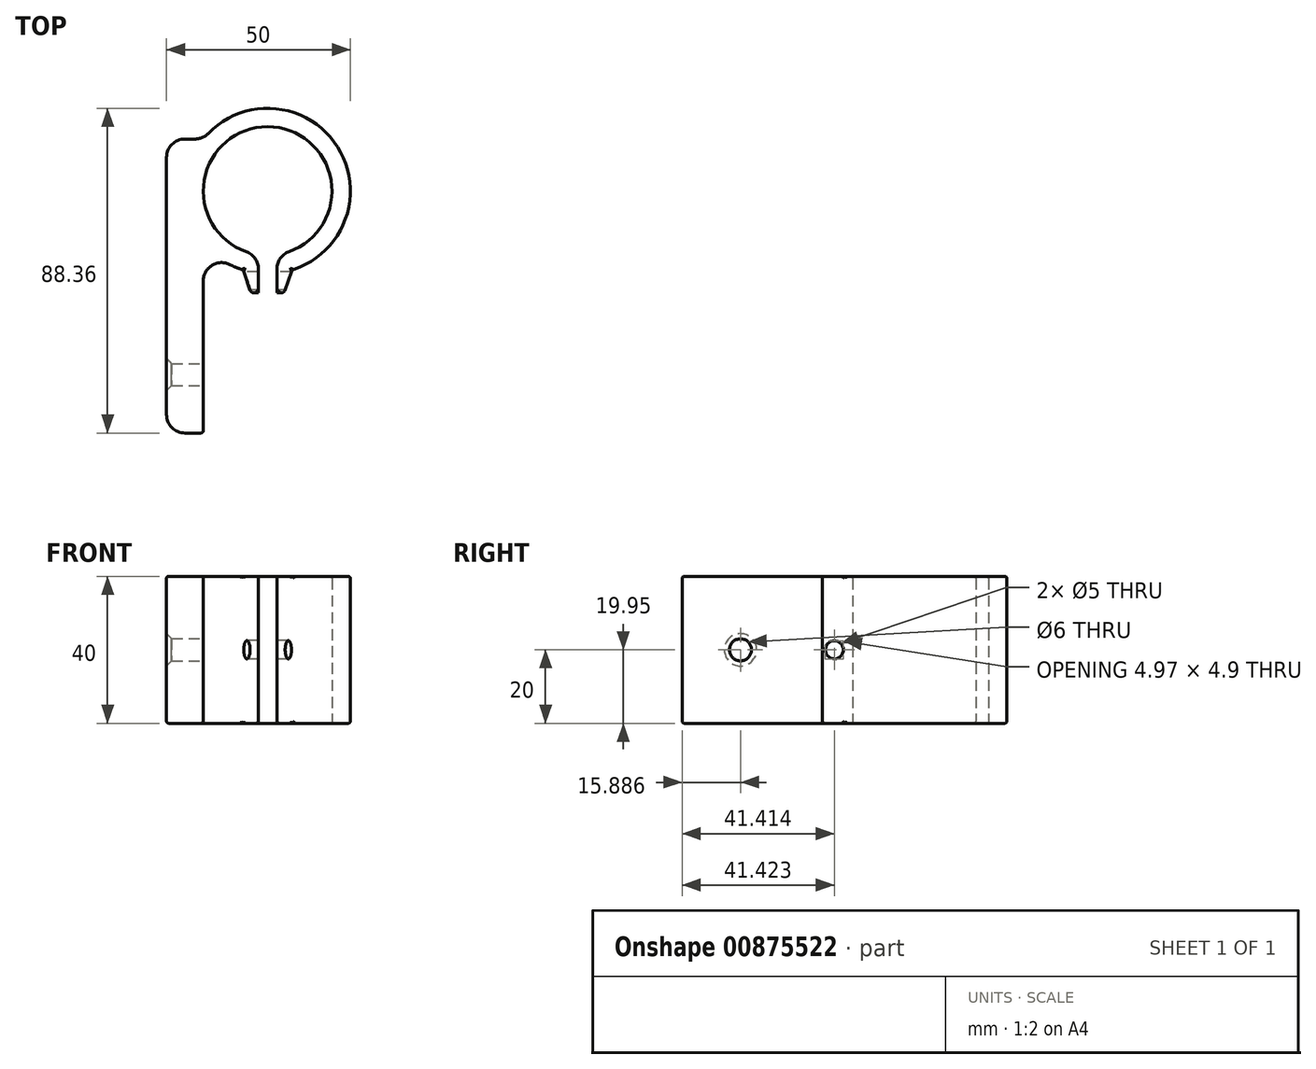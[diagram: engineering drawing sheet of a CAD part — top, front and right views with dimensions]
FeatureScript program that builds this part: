
annotation { "Feature Type Name" : "Feature", "Feature Type Description" : "" }
export const myFeature = defineFeature(function(context is Context, id is Id, definition is map)
    precondition{}
    {
        {
            var Q0;
            Q0=qCreatedBy(makeId("Top.planeOp"),FACE);
            var sketch = newSketch(context, id + "F0", { "sketchPlane" : qUnion([Q0])});
            skLineSegment(sketch, "E0.left", {"start": v(-72.65, -0.58) * mm, "end": v(-72.65, -1.73) * mm});
            skLineSegment(sketch, "E0.right", {"start": v(-77.68, -0.58) * mm, "end": v(-77.68, -7.05) * mm});
            skArc(sketch, "E1", {"start": v(-69.32, 4.13) * mm, "mid": v(-75.17, 38.13) * mm, "end": v(-81.01, 4.13) * mm});
            skLineSegment(sketch, "E2", {"start": v(-72.65, -1.73) * mm, "end": v(-72.65, -7.05) * mm});
            skArc(sketch, "E3", {"start": v(-72.65, -1.73) * mm, "mid": v(-54.97, 30.55) * mm, "end": v(-91.32, 36.29) * mm});
            skLineSegment(sketch, "E4", {"start": v(-72.65, -7.05) * mm, "end": v(-70.65, -7.05) * mm});
            skLineSegment(sketch, "E5", {"start": v(-77.68, -7.05) * mm, "end": v(-79.68, -7.05) * mm});
            skLineSegment(sketch, "E6", {"start": v(-79.68, -7.05) * mm, "end": v(-81.8, -0.87) * mm});
            skLineSegment(sketch, "E7", {"start": v(-70.65, -7.05) * mm, "end": v(-68.52, -0.87) * mm});
            skArc(sketch, "E8", {"start": v(-85.4, 0.59) * mm, "mid": v(-81.64, -0.92) * mm, "end": v(-77.68, -1.73) * mm});
            skLineSegment(sketch, "E9", {"start": v(-95.7, 11.42) * mm, "end": v(-95.7, 29.83) * mm});
            skLineSegment(sketch, "E10", {"start": v(-92.67, 20.63) * mm, "end": v(-92.67, 34.77) * mm});
            skPoint(sketch, "E10.startSnap0", {"position": v(-95.7, 20.63) * mm});
            skLineSegment(sketch, "E11", {"start": v(-92.67, 20.63) * mm, "end": v(-92.67, 6.49) * mm});
            skLineSegment(sketch, "E12.bottom", {"start": v(-94.91, 34.77) * mm, "end": v(-97.67, 34.77) * mm});
            skLineSegment(sketch, "E12.top", {"start": v(-92.67, -45.23) * mm, "end": v(-97.67, -45.23) * mm});
            skLineSegment(sketch, "E12.left", {"start": v(-92.67, -3.87) * mm, "end": v(-92.67, -45.23) * mm});
            skLineSegment(sketch, "E12.right", {"start": v(-102.67, 29.77) * mm, "end": v(-102.67, -40.23) * mm});
            skPoint(sketch, "E13.visualSharp", {"position": v(-102.67, 34.77) * mm});
            skArc(sketch, "E13.filletArc", {"start": v(-97.67, 34.77) * mm, "mid": v(-101.2, 33.3) * mm, "end": v(-102.67, 29.77) * mm});
            skArc(sketch, "E14.filletArc", {"start": v(-94.91, 34.77) * mm, "mid": v(-92.96, 35.17) * mm, "end": v(-91.32, 36.29) * mm});
            skArc(sketch, "E15.filletArc", {"start": v(-85.4, 0.59) * mm, "mid": v(-90.28, 0.4) * mm, "end": v(-92.67, -3.87) * mm});
            skPoint(sketch, "E16.visualSharp", {"position": v(-72.65, 3.31) * mm});
            skArc(sketch, "E16.filletArc", {"start": v(-69.32, 4.13) * mm, "mid": v(-71.73, 2.3) * mm, "end": v(-72.65, -0.58) * mm});
            skPoint(sketch, "E17.visualSharp", {"position": v(-77.68, 3.31) * mm});
            skArc(sketch, "E17.filletArc", {"start": v(-77.68, -0.58) * mm, "mid": v(-78.6, 2.3) * mm, "end": v(-81.01, 4.13) * mm});
            skPoint(sketch, "E18.visualSharp", {"position": v(-102.67, -45.23) * mm});
            skArc(sketch, "E18.filletArc", {"start": v(-102.67, -40.23) * mm, "mid": v(-101.2, -43.77) * mm, "end": v(-97.67, -45.23) * mm});
            skLineSegment(sketch, "E19.left", {"start": v(-92.67, -45.23) * mm, "end": v(-92.67, -41.23) * mm});
            skLineSegment(sketch, "E20.left", {"start": v(-92.67, -41.23) * mm, "end": v(-92.67, -16.23) * mm});
            skLineSegment(sketch, "E21.left", {"start": v(-92.67, -16.23) * mm, "end": v(-92.67, -12.23) * mm});
            skLineSegment(sketch, "E22.left", {"start": v(-92.67, -16.23) * mm, "end": v(-92.67, -41.23) * mm});
            skSolve(sketch);
        }
        {
            var Q0;
            {var subQ0=sQuery(id+"F0.wireOp",EDGE,"E5");Q0=makeQuery(id+"F0.imprint","IMPRINT",FACE,{"disambiguationData":[TD([[makeQuery(id+"F0.imprint","IMPRINT",EDGE,{"derivedFrom":subQ0}),-1.0]])]});}
            var Q1;
            {var subQ0=sQuery(id+"F0.wireOp",EDGE,"E2");Q1=makeQuery(id+"F0.imprint","IMPRINT",FACE,{"disambiguationData":[TD([[makeQuery(id+"F0.imprint","IMPRINT",EDGE,{"derivedFrom":subQ0}),1.0]])]});}
            var Q2;
            {var subQ6=sQuery(id+"F0.wireOp",EDGE,"E0.left");Q2=makeQuery(id+"F0.imprint","IMPRINT",FACE,{"disambiguationData":[TD([[makeQuery(id+"F0.imprint","IMPRINT",EDGE,{"derivedFrom":subQ6}),1.0]])]});}
            extrude(context, id + "F1", {"entities" : qUnion([Q0, Q1, Q2]), "depth" : 40 * mm, "offsetDistance" : 25 * mm});
        }
        {
            var Q0;
            Q0=makeQuery(id+"F1.opExtrude","CAP_FACE",FACE,{"disambiguationData":[OSD([sQuery(id+"F0.wireOp",EDGE,"E0.left"),sQuery(id+"F0.wireOp",EDGE,"E0.right"),sQuery(id+"F0.wireOp",EDGE,"E1"),sQuery(id+"F0.wireOp",EDGE,"E2"),sQuery(id+"F0.wireOp",EDGE,"E3"),sQuery(id+"F0.wireOp",EDGE,"E4"),sQuery(id+"F0.wireOp",EDGE,"E5"),sQuery(id+"F0.wireOp",EDGE,"E6"),sQuery(id+"F0.wireOp",EDGE,"E7"),sQuery(id+"F0.wireOp",EDGE,"E8"),sQuery(id+"F0.wireOp",EDGE,"E12.bottom"),sQuery(id+"F0.wireOp",EDGE,"E12.top"),sQuery(id+"F0.wireOp",EDGE,"E12.left"),sQuery(id+"F0.wireOp",EDGE,"E12.right"),sQuery(id+"F0.wireOp",EDGE,"E13.filletArc"),sQuery(id+"F0.wireOp",EDGE,"E14.filletArc"),sQuery(id+"F0.wireOp",EDGE,"E15.filletArc"),sQuery(id+"F0.wireOp",EDGE,"E16.filletArc"),sQuery(id+"F0.wireOp",EDGE,"E17.filletArc"),sQuery(id+"F0.wireOp",EDGE,"E18.filletArc"),sQuery(id+"F0.wireOp",EDGE,"E19.left"),sQuery(id+"F0.wireOp",EDGE,"E21.left"),sQuery(id+"F0.wireOp",EDGE,"E22.left")])],"isStart":false});
            fillet(context, id + "F2", {"entities" : qUnion([Q0]), "radius" : .6 * mm, "tangentPropagation" : true, "allowEdgeOverflow" : false});
        }
        {
            var Q0;
            Q0=makeQuery(id+"F1.opExtrude","CAP_FACE",FACE,{"disambiguationData":[OSD([sQuery(id+"F0.wireOp",EDGE,"E0.left"),sQuery(id+"F0.wireOp",EDGE,"E0.right"),sQuery(id+"F0.wireOp",EDGE,"E1"),sQuery(id+"F0.wireOp",EDGE,"E2"),sQuery(id+"F0.wireOp",EDGE,"E3"),sQuery(id+"F0.wireOp",EDGE,"E4"),sQuery(id+"F0.wireOp",EDGE,"E5"),sQuery(id+"F0.wireOp",EDGE,"E6"),sQuery(id+"F0.wireOp",EDGE,"E7"),sQuery(id+"F0.wireOp",EDGE,"E8"),sQuery(id+"F0.wireOp",EDGE,"E12.bottom"),sQuery(id+"F0.wireOp",EDGE,"E12.top"),sQuery(id+"F0.wireOp",EDGE,"E12.left"),sQuery(id+"F0.wireOp",EDGE,"E12.right"),sQuery(id+"F0.wireOp",EDGE,"E13.filletArc"),sQuery(id+"F0.wireOp",EDGE,"E14.filletArc"),sQuery(id+"F0.wireOp",EDGE,"E15.filletArc"),sQuery(id+"F0.wireOp",EDGE,"E16.filletArc"),sQuery(id+"F0.wireOp",EDGE,"E17.filletArc"),sQuery(id+"F0.wireOp",EDGE,"E18.filletArc"),sQuery(id+"F0.wireOp",EDGE,"E19.left"),sQuery(id+"F0.wireOp",EDGE,"E21.left"),sQuery(id+"F0.wireOp",EDGE,"E22.left")])],"isStart":true});
            var Q1;
            Q1=makeQuery(id+"F1.opExtrude","SWEPT_EDGE",EDGE,{"disambiguationData":[OSD([sQuery(id+"F0.wireOp",EDGE,"E12.top"),sQuery(id+"F0.wireOp",EDGE,"E19.left")])]});
            fillet(context, id + "F3", {"entities" : qUnion([Q0, Q1]), "radius" : .6 * mm, "tangentPropagation" : true, "allowEdgeOverflow" : false});
        }
        {
            var Q0;
            Q0=makeQuery(id+"F1.opExtrude","SWEPT_EDGE",EDGE,{"disambiguationData":[OSD([sQuery(id+"F0.wireOp",EDGE,"E3"),sQuery(id+"F0.wireOp",EDGE,"E7")])]});
            var Q1;
            Q1=makeQuery(id+"F1.opExtrude","SWEPT_EDGE",EDGE,{"disambiguationData":[OSD([sQuery(id+"F0.wireOp",EDGE,"E6"),sQuery(id+"F0.wireOp",EDGE,"E8")])]});
            var Q2;
            Q2=makeQuery(id+"F1.opExtrude","SWEPT_EDGE",EDGE,{"disambiguationData":[OSD([sQuery(id+"F0.wireOp",EDGE,"E5"),sQuery(id+"F0.wireOp",EDGE,"E6")])]});
            var Q3;
            Q3=makeQuery(id+"F1.opExtrude","SWEPT_EDGE",EDGE,{"disambiguationData":[OSD([sQuery(id+"F0.wireOp",EDGE,"E4"),sQuery(id+"F0.wireOp",EDGE,"E7")])]});
            fillet(context, id + "F4", {"entities" : qUnion([Q0, Q1, Q2, Q3]), "radius" : 1 * mm, "tangentPropagation" : true, "allowEdgeOverflow" : false});
        }
        {
            var Q0;
            Q0=makeQuery(id+"F1.opExtrude","SWEPT_FACE",FACE,{"disambiguationData":[OSD([sQuery(id+"F0.wireOp",EDGE,"E12.left"),sQuery(id+"F0.wireOp",EDGE,"E19.left"),sQuery(id+"F0.wireOp",EDGE,"E21.left"),sQuery(id+"F0.wireOp",EDGE,"E22.left")])]});
            var sketch = newSketch(context, id + "F5", { "sketchPlane" : qUnion([Q0])});
            skPoint(sketch, "E23.endSnap0", {"position": v(-24.25, 39.4) * mm});
            skCircle(sketch, "E24", {"center": v(-29.34, 20) * mm, "radius": 3 * mm});
            skSolve(sketch);
        }
        {
            var Q0;
            Q0=makeQuery(id+"F5.imprint","IMPRINT",FACE,{"disambiguationData":[TD([[makeQuery(id+"F5.imprint","IMPRINT",EDGE,{"derivedFrom":sQuery(id+"F5.wireOp",EDGE,"E24")}),1.0]])]});
            extrude(context, id + "F6", {"entities" : qUnion([Q0]), "operationType" : NewBodyOperationType.REMOVE, "oppositeDirection" : true, "depth" : 25 * mm, "offsetDistance" : 25 * mm});
        }
        {
            var Q0;
            Q0=makeQuery(id+"F6.boolean.opBoolean","INTERSECT",EDGE,{"derivedFrom":[makeQuery(id+"F1.opExtrude","SWEPT_FACE",FACE,{"disambiguationData":[OSD([sQuery(id+"F0.wireOp",EDGE,"E12.right")])]}),makeQuery(id+"F6.opExtrude","SWEPT_FACE",FACE,{"disambiguationData":[OSD([sQuery(id+"F5.wireOp",EDGE,"E24")])]})]});
            chamfer(context, id + "F7", {"entities" : qUnion([Q0]), "width" : 1.4 * mm, "tangentPropagation" : true});
        }
        {
            var Q0;
            Q0=makeQuery(id+"F1.opExtrude","SWEPT_FACE",FACE,{"disambiguationData":[OSD([sQuery(id+"F0.wireOp",EDGE,"E0.right")])]});
            var sketch = newSketch(context, id + "F8", { "sketchPlane" : qUnion([Q0])});
            skLineSegment(sketch, "E25", {"start": v(-3.82, 0.6) * mm, "end": v(-3.82, 20) * mm});
            skPoint(sketch, "E25.endSnap0", {"position": v(-7.05, 20) * mm});
            skCircle(sketch, "E26", {"center": v(-3.82, 20) * mm, "radius": 2.5 * mm});
            skSolve(sketch);
        }
        {
            var Q0;
            Q0=makeQuery(id+"F8.imprint","IMPRINT",FACE,{"disambiguationData":[TD([[makeQuery(id+"F8.imprint","IMPRINT",EDGE,{"derivedFrom":sQuery(id+"F8.wireOp",EDGE,"E26")}),1.0]])]});
            extrude(context, id + "F9", {"entities" : qUnion([Q0]), "operationType" : NewBodyOperationType.REMOVE, "endBound" : BoundingType.SYMMETRIC, "depth" : 20.8 * mm, "offsetDistance" : 25 * mm});
        }
    });
